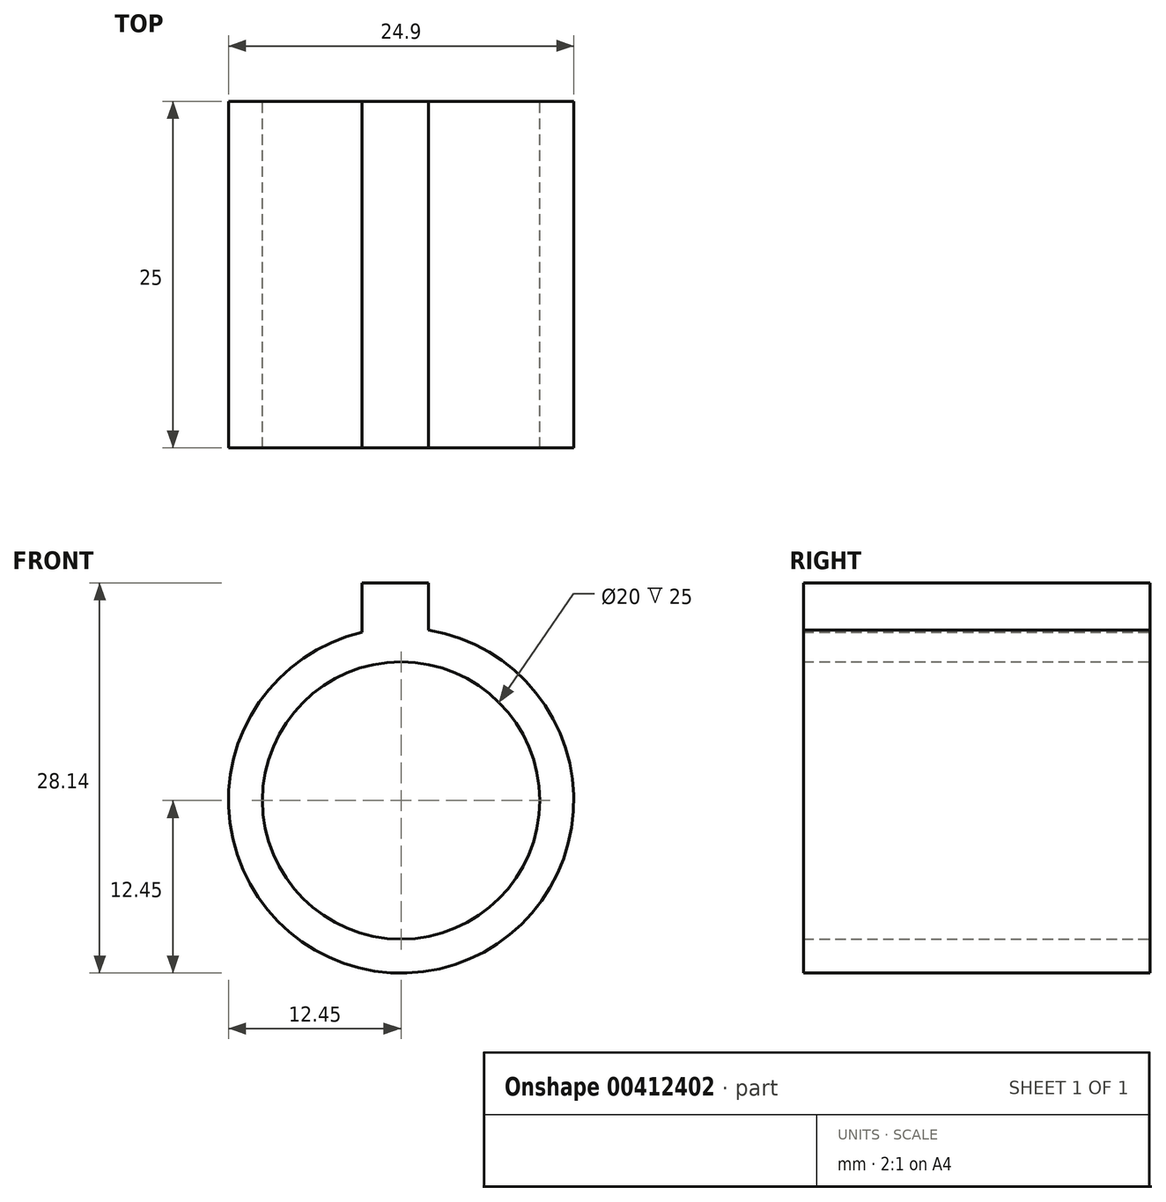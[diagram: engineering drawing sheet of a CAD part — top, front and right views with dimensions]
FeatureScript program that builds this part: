
annotation { "Feature Type Name" : "Feature", "Feature Type Description" : "" }
export const myFeature = defineFeature(function(context is Context, id is Id, definition is map)
    precondition{}
    {
        {
            var Q0;
            Q0=qCreatedBy(makeId("Front.planeOp"),FACE);
            var sketch = newSketch(context, id + "F0", { "sketchPlane" : qUnion([Q0])});
            skArc(sketch, "E0", {"start": v(-2.81, 12.13) * mm, "mid": v(0.42, -12.44) * mm, "end": v(1.99, 12.3) * mm});
            skLineSegment(sketch, "E1.top", {"start": v(1.99, 15.7) * mm, "end": v(-2.81, 15.7) * mm});
            skLineSegment(sketch, "E1.left", {"start": v(1.99, 12.3) * mm, "end": v(1.99, 15.7) * mm});
            skLineSegment(sketch, "E1.right", {"start": v(-2.81, 12.13) * mm, "end": v(-2.81, 15.7) * mm});
            skPoint(sketch, "E1.middle", {"position": v(-0.41, 12.44) * mm});
            skPoint(sketch, "E2.orphan", {"position": v(-2.81, 9.2) * mm});
            skPoint(sketch, "E3.orphan", {"position": v(1.99, 9.2) * mm});
            skCircle(sketch, "E4", {"center": v(0, 0) * mm, "radius": 10 * mm});
            skSolve(sketch);
        }
        {
            var Q0;
            Q0=makeQuery(id+"F0.imprint","IMPRINT",FACE,{"disambiguationData":[TD([[makeQuery(id+"F0.imprint","IMPRINT",EDGE,{"derivedFrom":sQuery(id+"F0.wireOp",EDGE,"E0")}),1.0]])]});
            extrude(context, id + "F1", {"entities" : qUnion([Q0]), "depth" : 25 * mm, "offsetDistance" : 25 * mm});
        }
    });
